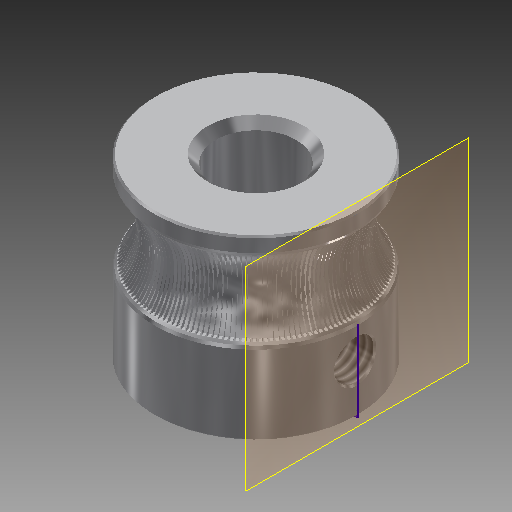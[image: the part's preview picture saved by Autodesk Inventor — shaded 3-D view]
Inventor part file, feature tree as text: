
AUTODESK INVENTOR PART (.ipt)
format: ipt  version: 2018 (Build 220112000, 112)  size: 3,500,032 bytes
history: native  units: mm
features: sketch x5, other x3, chamfer x3, hole x2, revolve x1, pattern_circular x1
ambient origin geometry x8: Origin, YZ Plane, XZ Plane, XY Plane, X Axis, Y Axis, Z Axis, Center Point
bodies: Body1 (feature_tree)
feature tree (15):
  other  "Bryła1"
  revolve  "Obrót1"
  chamfer  "Faza1"  Distance=6.3mm
  hole  "Otwór1"  [1 undecoded]
  chamfer  "Faza2"  Distance=5.0mm
  sketch  "Szkic4"
  other  "Płaszczyzna konstrukcyjna1"
  hole  "Otwór2"  [1 undecoded]
  chamfer  "Faza3"  Distance=5.3mm
  other  "Wypukłość2"
  pattern_circular  "Szyk kołowy3"  [2 undecoded]
  sketch  "Szkic1"
  sketch  "Szkic3"
  sketch  "Szkic5"
  sketch  "Szkic7"
note: 4 required parameter values undecoded (feature->parameter linkage not recoverable at this tier; creation-order binding heuristic only, values carry confidence <= 0.55)
